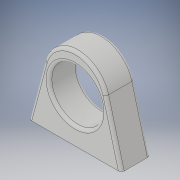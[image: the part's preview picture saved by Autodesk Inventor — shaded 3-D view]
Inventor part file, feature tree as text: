
AUTODESK INVENTOR PART (.ipt)
format: ipt  version: 2018 (Build 220112000, 112)  size: 177,152 bytes
history: native  units: in
note: dims shown in document units (in); Inventor stores cm internally (conversion verified against a paired STEP export)
features: other x3, extrude x3, sketch x3, chamfer x2, fillet x2
ambient origin geometry x8: Origin, YZ Plane, XZ Plane, XY Plane, X Axis, Y Axis, Z Axis, Center Point
bodies: Solid1 (feature_tree)
feature tree (13):
  other  "Annotations"
  extrude  "Extrusion1"  Depth=1.0in
  extrude  "Extrusion2"  Depth=1.0in
  chamfer  "Chamfer1"  Distance=1.0in
  chamfer  "Chamfer2"  Distance=0.8in Angle=45.0deg
  fillet  "Fillet1"  Radius=1.1in
  fillet  "Fillet2"  Radius=0.1in
  extrude  "Extrusion4"  Depth=0.48in
  sketch  "Sketch2"  dims[d2=3.2in d3=1.0in]
  sketch  "Sketch3"  dims[d4=3.0in d5=0.0in d6=1.8in d7=1.0in d8=0.0in d9=0.8in d10=3.0in d11=45.0deg]
  sketch  "Sketch5"  dims[d12=0.8in d13=3.0in d14=45.0deg d15=1.1in d16=0.1in d23=0.41in d24=0.24in d25=0.82in d26=0.48in d27=0.2in d28=0.0in d29=0.25in d30=0.2509in d31=0.82in d32=0.1756in d33=0.1228in d34=0.48in]
  other  "Linear Dimension 1"
  other  "Linear Dimension 2"
